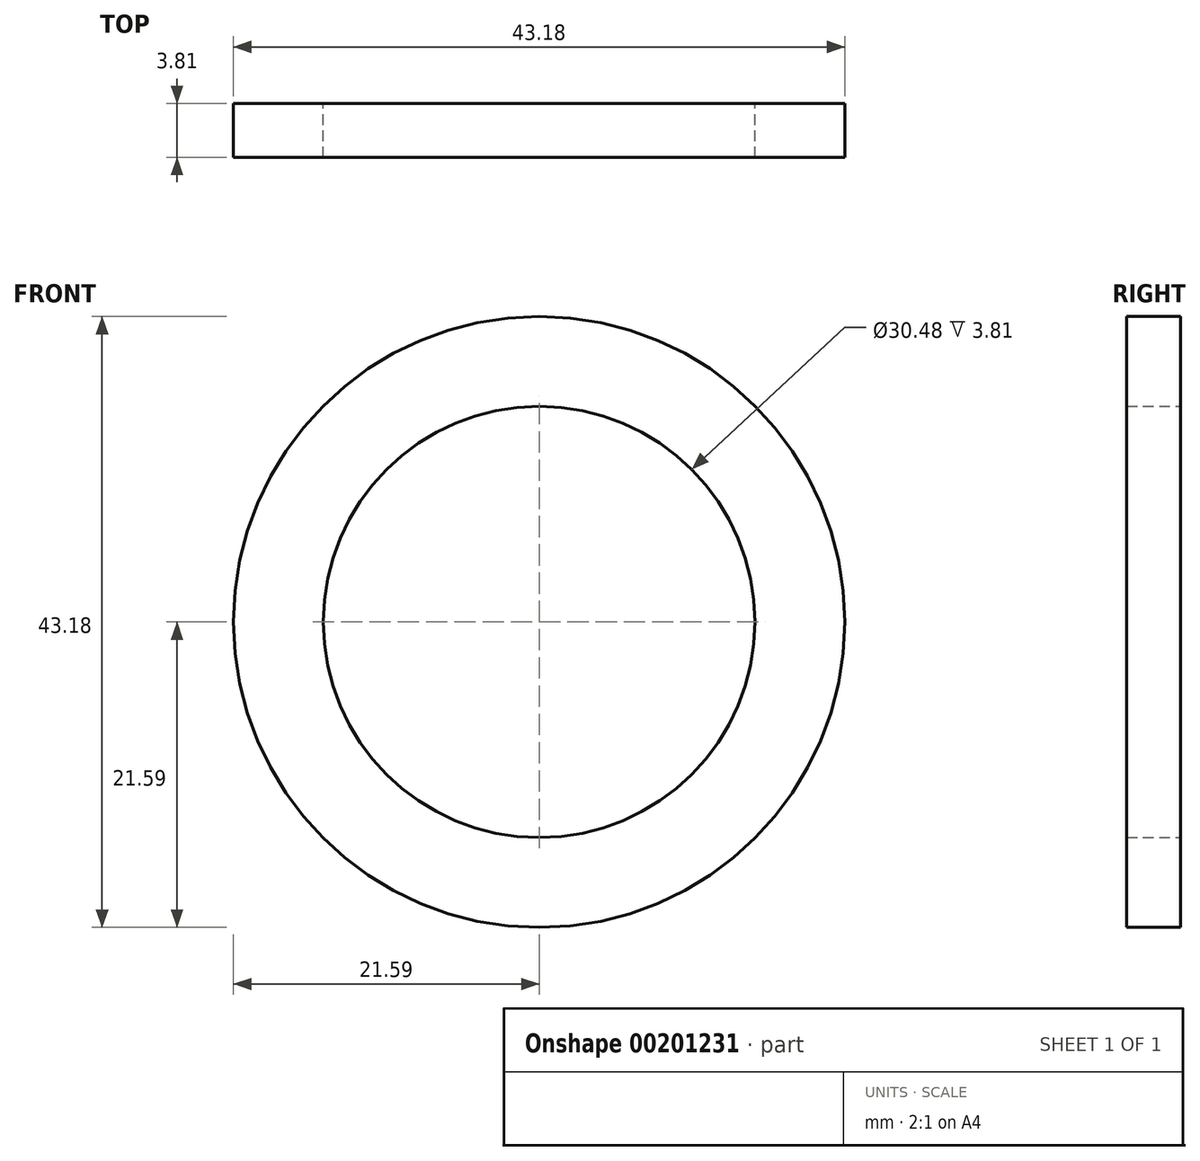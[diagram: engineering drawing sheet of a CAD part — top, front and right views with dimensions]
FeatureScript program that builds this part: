
annotation { "Feature Type Name" : "Feature", "Feature Type Description" : "" }
export const myFeature = defineFeature(function(context is Context, id is Id, definition is map)
    precondition{}
    {
        {
            var Q0;
            Q0=qCreatedBy(makeId("Front.planeOp"),FACE);
            var sketch = newSketch(context, id + "F0", { "sketchPlane" : qUnion([Q0])});
            skCircle(sketch, "E0", {"center": v(0, 0) * mm, "radius": 21.59 * mm});
            skCircle(sketch, "E1", {"center": v(0, 0) * mm, "radius": 15.24 * mm});
            skSolve(sketch);
        }
        {
            var Q0;
            Q0=makeQuery(id+"F0.imprint","IMPRINT",FACE,{"disambiguationData":[TD([[makeQuery(id+"F0.imprint","IMPRINT",EDGE,{"derivedFrom":sQuery(id+"F0.wireOp",EDGE,"E0")}),1.0]])]});
            extrude(context, id + "F1", {"entities" : qUnion([Q0]), "depth" : 3.8 * mm});
        }
    });
